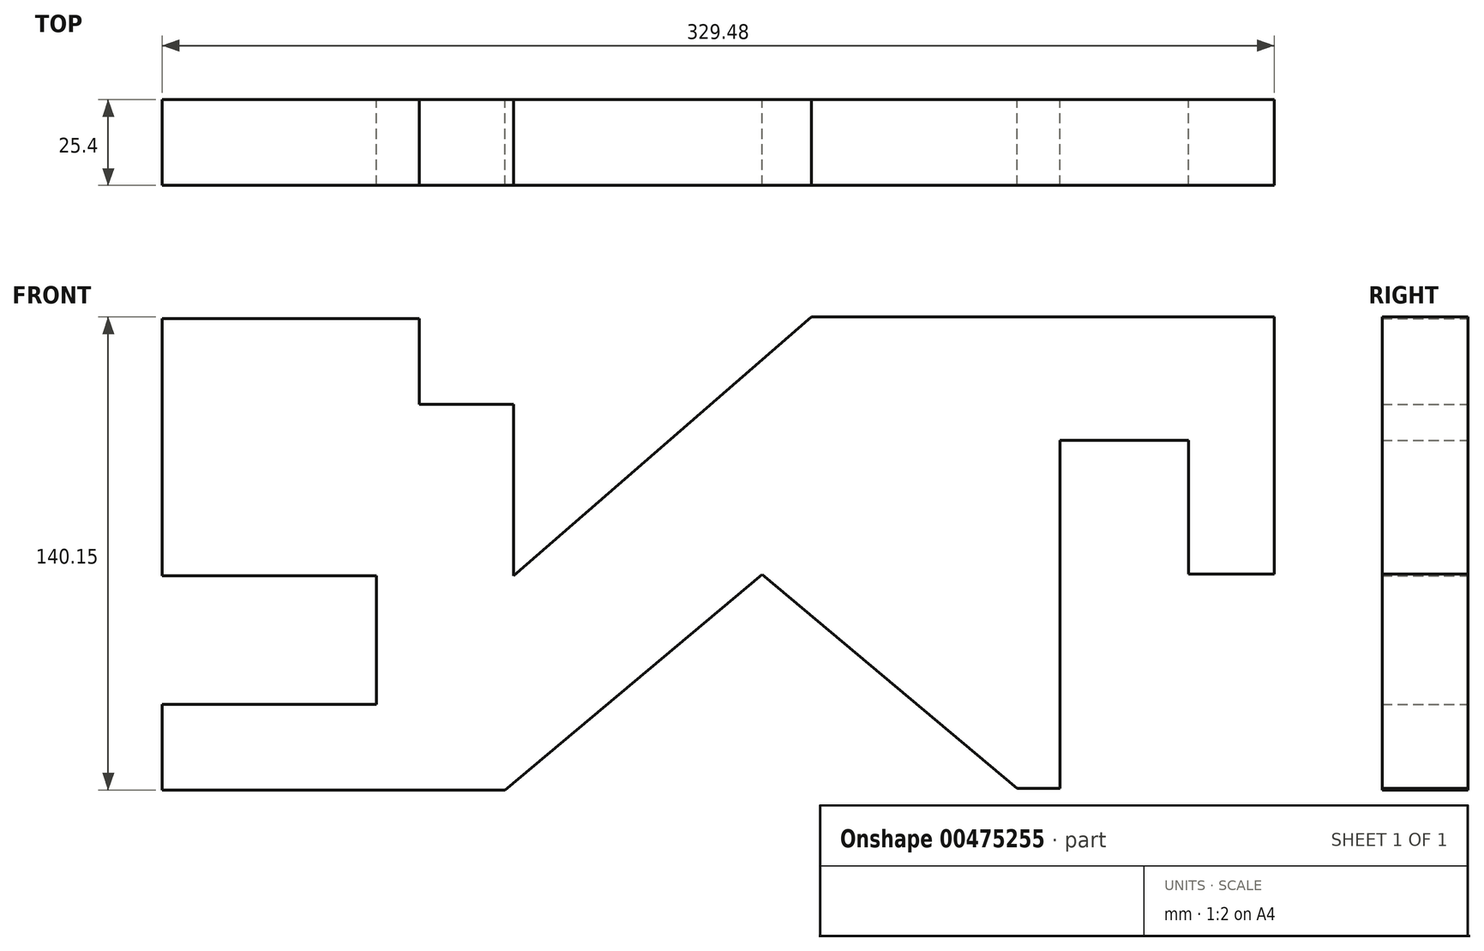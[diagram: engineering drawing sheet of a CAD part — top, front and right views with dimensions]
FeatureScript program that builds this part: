
annotation { "Feature Type Name" : "Feature", "Feature Type Description" : "" }
export const myFeature = defineFeature(function(context is Context, id is Id, definition is map)
    precondition{}
    {
        {
            var Q0;
            Q0=qCreatedBy(makeId("Front.planeOp"),FACE);
            var sketch = newSketch(context, id + "F0", { "sketchPlane" : qUnion([Q0])});
            skLineSegment(sketch, "E0", {"start": v(-76.2, 76.2) * mm, "end": v(-76.2, 0) * mm});
            skLineSegment(sketch, "E1", {"start": v(-76.2, 0) * mm, "end": v(-12.7, 0) * mm});
            skLineSegment(sketch, "E2", {"start": v(-12.7, 0) * mm, "end": v(-12.7, -38.1) * mm});
            skLineSegment(sketch, "E3", {"start": v(-12.7, -38.1) * mm, "end": v(-76.2, -38.1) * mm});
            skLineSegment(sketch, "E4", {"start": v(-76.2, -38.1) * mm, "end": v(-76.2, -63.5) * mm});
            skLineSegment(sketch, "E5", {"start": v(-76.2, -63.5) * mm, "end": v(25.4, -63.5) * mm});
            skLineSegment(sketch, "E6", {"start": v(-76.2, 76.2) * mm, "end": v(0, 76.2) * mm});
            skLineSegment(sketch, "E7", {"start": v(0, 76.2) * mm, "end": v(0, 50.8) * mm});
            skLineSegment(sketch, "E8", {"start": v(0, 50.8) * mm, "end": v(27.94, 50.8) * mm});
            skLineSegment(sketch, "E9", {"start": v(27.94, 50.8) * mm, "end": v(27.94, 0) * mm});
            skLineSegment(sketch, "E10", {"start": v(27.94, 0) * mm, "end": v(116.12, 76.65) * mm});
            skLineSegment(sketch, "E11", {"start": v(116.12, 76.65) * mm, "end": v(253.28, 76.65) * mm});
            skLineSegment(sketch, "E12", {"start": v(253.28, 76.65) * mm, "end": v(253.28, 0.45) * mm});
            skLineSegment(sketch, "E13", {"start": v(253.28, 0.45) * mm, "end": v(227.88, 0.45) * mm});
            skLineSegment(sketch, "E14", {"start": v(227.88, 0.45) * mm, "end": v(227.88, 40.14) * mm});
            skLineSegment(sketch, "E15", {"start": v(227.88, 40.14) * mm, "end": v(189.78, 40.14) * mm});
            skLineSegment(sketch, "E16", {"start": v(189.78, 40.14) * mm, "end": v(189.78, -63.05) * mm});
            skLineSegment(sketch, "E17", {"start": v(189.78, -63.05) * mm, "end": v(177.08, -63.05) * mm});
            skLineSegment(sketch, "E18", {"start": v(177.08, -63.05) * mm, "end": v(101.51, 0.36) * mm});
            skLineSegment(sketch, "E19", {"start": v(101.51, 0.36) * mm, "end": v(25.4, -63.5) * mm});
            skLineSegment(sketch, "E20", {"start": v(25.4, -63.5) * mm, "end": v(46.57, -63.5) * mm});
            skSolve(sketch);
        }
        {
            var Q0;
            Q0=makeQuery(id+"F0.imprint","IMPRINT",FACE,{"disambiguationData":[TD([[makeQuery(id+"F0.imprint","IMPRINT",EDGE,{"derivedFrom":sQuery(id+"F0.wireOp",EDGE,"E0")}),1.0]])]});
            extrude(context, id + "F1", {"entities" : qUnion([Q0]), "depth" : 25.4 * mm});
        }
    });
